# Revit family: Tub_Filler-DXV-Fitzgerald-D35160980_Series
name_source: partatom
category: Plumbing Fixtures
revit_build: Autodesk Revit 2014 (Build: 20130308_1515(x64)
units: mm (PartAtom-declared; Revit-internal decimal feet)

## types (3) — shared parameters
Assembly Code = D2020300
CW Connection = Yes
CWFU = 3
Cold Water Connection Diameter = 1/2"
Cold Water Connection Radius = 1/4"
Cold Water Connection Width = 3"
Default Elevation = 34"
Description = Fitzgerald Wall Mount Tub Filler
Flow Rate = 1.8 gpm (6.8 L/min)
HW Connection = Yes
HWFU = 3
Height = 11 3/4"
Hot Water Connection Diameter = 1"
Hot Water Connection Radius = 1/4"
Hot Water Connection Width = 3"
Installation Type = Wall Mounted
Length = 7 3/4"
Manufacturer = DXV
Price = Prices may vary. Please consult Manufacturer Representative for most up-to-date price list.
Product Documentation Link = https://dxv01.blob.core.windows.net
Product Page URL = https://www.dxv.com
URL = www.dxv.com
Vent Connection = No
WFU = 4
Waste Connection = No
Width = 11 11/16"

## per-type parameters (varying)
| type | Finish | Material |
| D35000981.100 | Cast Brass-DXV-100-Polished Chrome | Cast Brass-DXV-100-Polished Chrome |
| D35000981.144 | Cast Brass-DXV-144-Brushed Nickel | Cast Brass-DXV-144-Brushed Nickel |
| D35000981.150 | Cast Brass-DXV-150-Platinum-Nickel | Cast Brass-DXV-150-Platinum-Nickel |

note: column(s) folded — value = type name in every type: Model

## geometry (parser evidence)
native form markers: Sweep x2
no freeform markers — native parametric forms only
